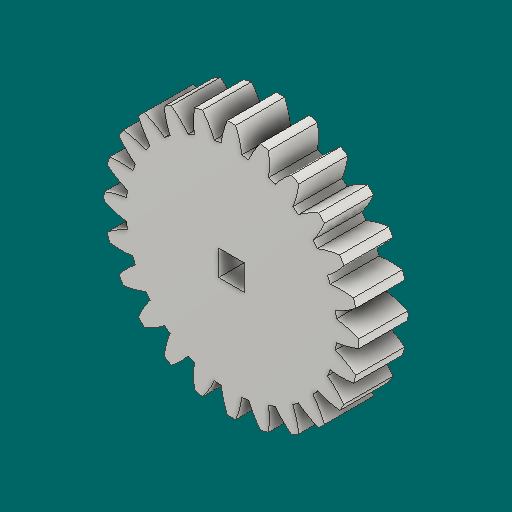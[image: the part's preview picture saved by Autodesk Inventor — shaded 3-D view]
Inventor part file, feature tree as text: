
AUTODESK INVENTOR PART (.ipt)
format: ipt  version: 2023.1 (Build 271208000, 208)  size: 289,280 bytes
history: native  units: in
note: dims shown in document units (in); Inventor stores cm internally (conversion verified against a paired STEP export)
features: other x12, sketch x3, plane x3
ambient origin geometry x8: Origin, YZ Plane, XZ Plane, XY Plane, X Axis, Y Axis, Z Axis, Center Point
bodies: Solid1 (feature_tree)
feature tree (18):
  other  "Spur Gear13_MIR.ipt"
  other  "Solid1::Spur Gear13_MIR.ipt"
  other  "TaggingFeature1"
  sketch  "Sketch1"  dims[d0=0.3937in]
  sketch  "Sketch2"  dims[d9=0.0in]
  sketch  "Sketch3"  dims[d14=0.0in d15=1.2in d16=0.0in d17=0.0in d18=0.0in d19=1.2in]
  plane  "XZ Plane_1"
  plane  "Work Plane2"
  plane  "Work Plane3"
  other  "Srf1"
  other  "Srf1::Derived"
  other  "Start plane iMate"
  other  "Distance iMate"
  other  "Position iMate"
  other  "Mesh iMate"
  other  "Axis iMate"
  other  "Mesh iMate2"
  other  "Align iMate"
